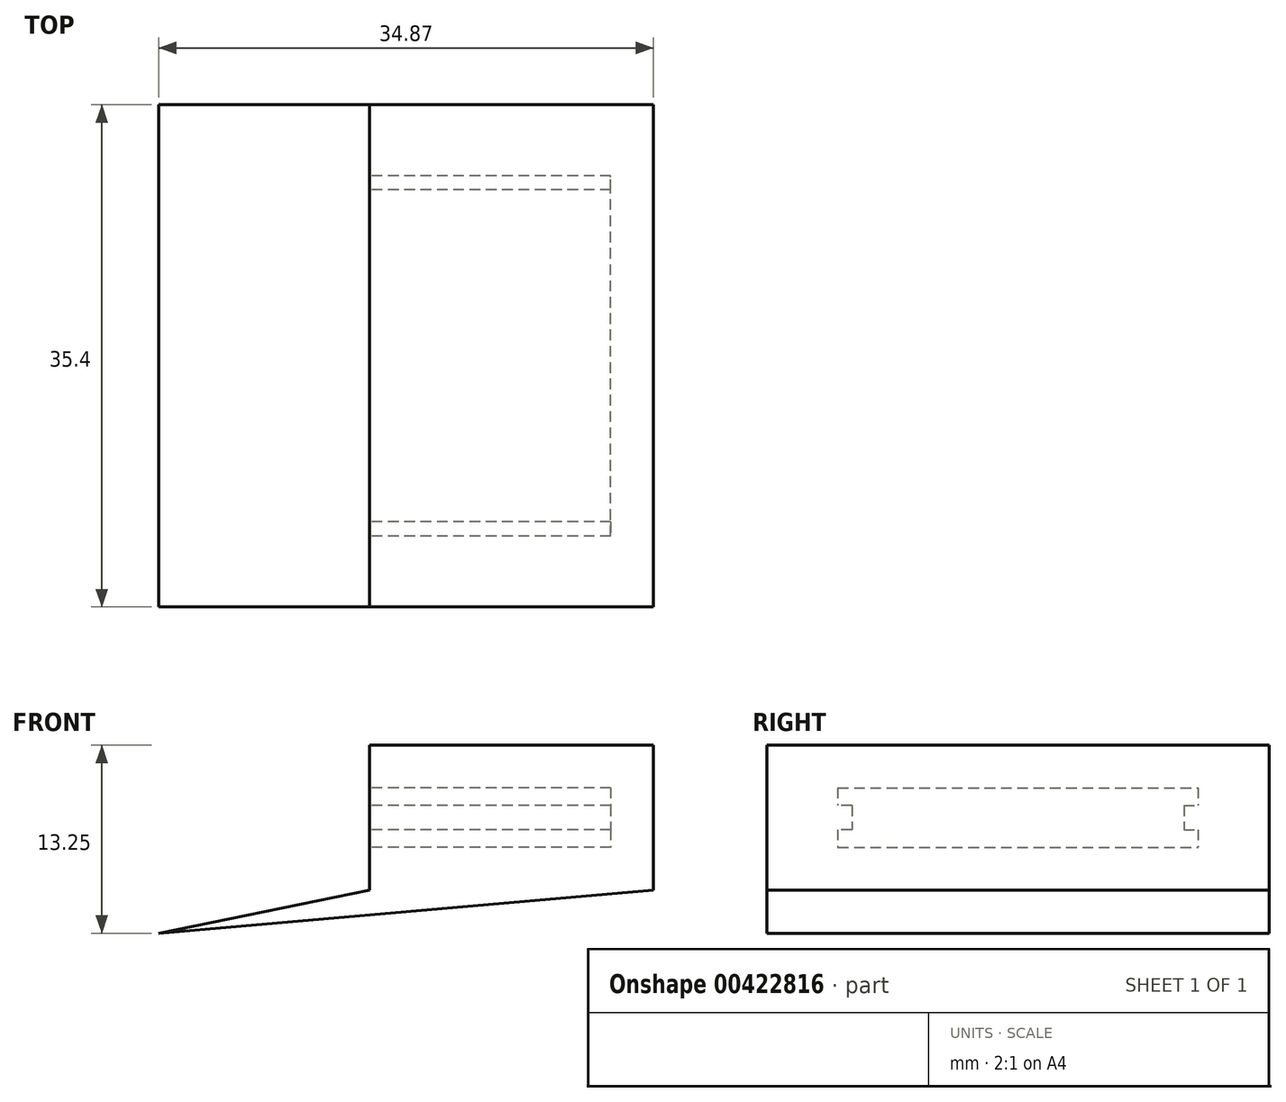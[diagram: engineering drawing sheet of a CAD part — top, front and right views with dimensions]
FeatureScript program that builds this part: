
annotation { "Feature Type Name" : "Feature", "Feature Type Description" : "" }
export const myFeature = defineFeature(function(context is Context, id is Id, definition is map)
    precondition{}
    {
        {
            var Q0;
            Q0=qCreatedBy(makeId("Top.planeOp"),FACE);
            var sketch = newSketch(context, id + "F0", { "sketchPlane" : qUnion([Q0])});
            skLineSegment(sketch, "E0.bottom", {"start": v(0, 0) * mm, "end": v(-20, 0) * mm});
            skLineSegment(sketch, "E0.top", {"start": v(0, 35.4) * mm, "end": v(-20, 35.4) * mm});
            skLineSegment(sketch, "E0.left", {"start": v(0, 0) * mm, "end": v(0, 35.4) * mm});
            skLineSegment(sketch, "E0.right", {"start": v(-20, 0) * mm, "end": v(-20, 35.4) * mm});
            skSolve(sketch);
        }
        {
            var Q0;
            Q0=qSketchRegion(id+"F0",true);
            extrude(context, id + "F1", {"entities" : qUnion([Q0]), "depth" : 10.2 * mm});
        }
        {
            var Q0;
            Q0=makeQuery(id+"F1.opExtrude","SWEPT_FACE",FACE,{"disambiguationData":[OSD([sQuery(id+"F0.wireOp",EDGE,"E0.right")])]});
            var sketch = newSketch(context, id + "F2", { "sketchPlane" : qUnion([Q0])});
            skLineSegment(sketch, "E1.bottom", {"start": v(-5, 7.2) * mm, "end": v(-30.4, 7.2) * mm});
            skLineSegment(sketch, "E1.top", {"start": v(-5, 3) * mm, "end": v(-30.4, 3) * mm});
            skLineSegment(sketch, "E1.left", {"start": v(-5, 7.2) * mm, "end": v(-5, 3) * mm});
            skLineSegment(sketch, "E1.right", {"start": v(-30.4, 7.2) * mm, "end": v(-30.4, 3) * mm});
            skLineSegment(sketch, "E2.bottom", {"start": v(-6, 5.95) * mm, "end": v(-5, 5.95) * mm});
            skLineSegment(sketch, "E2.top", {"start": v(-6, 4.25) * mm, "end": v(-5, 4.25) * mm});
            skLineSegment(sketch, "E2.left", {"start": v(-6, 5.95) * mm, "end": v(-6, 4.25) * mm});
            skLineSegment(sketch, "E2.right", {"start": v(-5, 5.95) * mm, "end": v(-5, 4.25) * mm});
            skPoint(sketch, "E3.oppositeSnap0", {"position": v(-5.5, 4.25) * mm});
            skLineSegment(sketch, "E3.bottom", {"start": v(-29.4, 5.95) * mm, "end": v(-30.4, 5.95) * mm});
            skLineSegment(sketch, "E3.top", {"start": v(-29.4, 4.25) * mm, "end": v(-30.4, 4.25) * mm});
            skLineSegment(sketch, "E3.left", {"start": v(-29.4, 5.95) * mm, "end": v(-29.4, 4.25) * mm});
            skLineSegment(sketch, "E3.right", {"start": v(-30.4, 5.95) * mm, "end": v(-30.4, 4.25) * mm});
            skSolve(sketch);
        }
        {
            var Q0;
            {var subQ7=sQuery(id+"F2.wireOp",EDGE,"E1.bottom");Q0=makeQuery(id+"F2.imprint","IMPRINT",FACE,{"disambiguationData":[TD([[makeQuery(id+"F2.imprint","IMPRINT",EDGE,{"derivedFrom":subQ7}),1.0]])]});}
            extrude(context, id + "F3", {"entities" : qUnion([Q0]), "operationType" : NewBodyOperationType.REMOVE, "oppositeDirection" : true, "depth" : 17 * mm});
        }
        {
            var Q0;
            Q0=makeQuery(id+"F1.opExtrude","SWEPT_FACE",FACE,{"disambiguationData":[OSD([sQuery(id+"F0.wireOp",EDGE,"E0.bottom")])]});
            var sketch = newSketch(context, id + "F4", { "sketchPlane" : qUnion([Q0])});
            skLineSegment(sketch, "E4", {"start": v(0, 0) * mm, "end": v(-34.87, -3.05) * mm});
            skLineSegment(sketch, "E5", {"start": v(-20, 0) * mm, "end": v(-34.87, -3.05) * mm});
            skSolve(sketch);
        }
        {
            var Q0;
            Q0=makeQuery(id+"F4.imprint","IMPRINT",FACE,{"disambiguationData":[TD([[makeQuery(id+"F4.imprint","IMPRINT",EDGE,{"derivedFrom":sQuery(id+"F4.wireOp",EDGE,"E5")}),1.0]])]});
            extrude(context, id + "F5", {"entities" : qUnion([Q0]), "operationType" : NewBodyOperationType.ADD, "oppositeDirection" : true, "depth" : 35.4 * mm});
        }
    });
